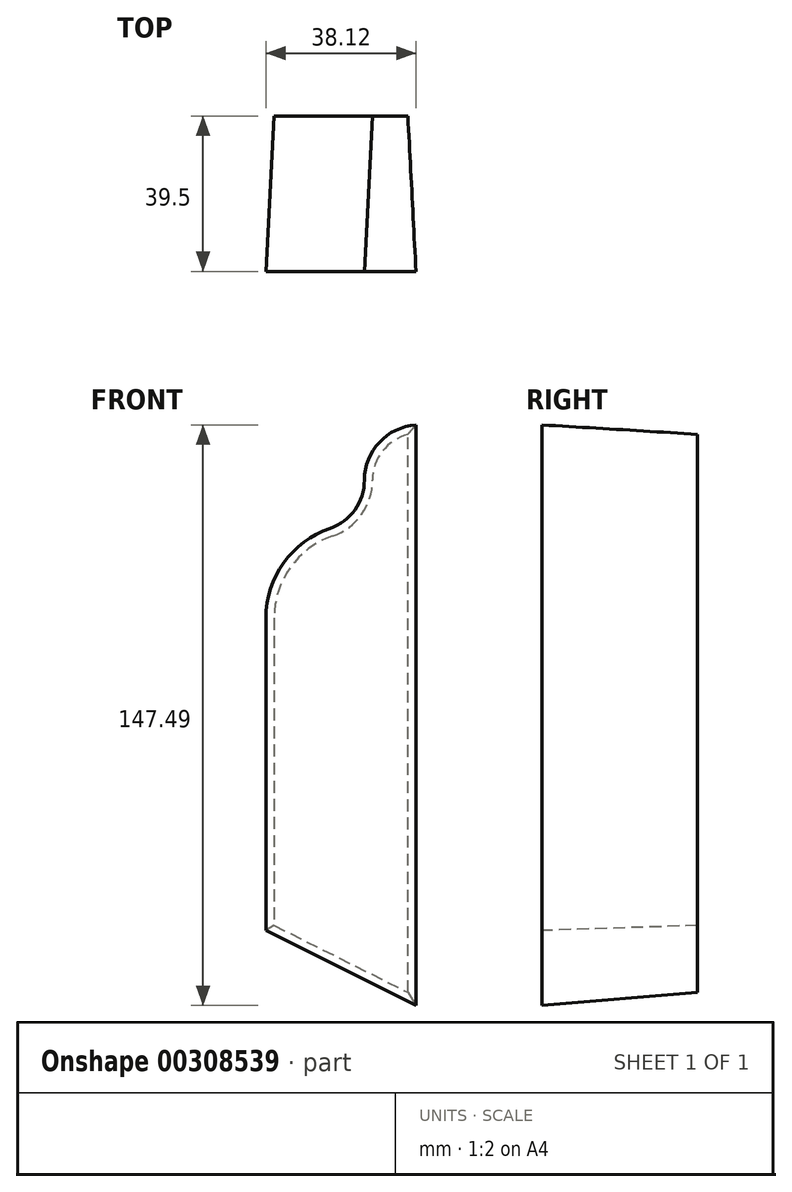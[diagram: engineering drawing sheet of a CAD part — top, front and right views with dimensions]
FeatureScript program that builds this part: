
annotation { "Feature Type Name" : "Feature", "Feature Type Description" : "" }
export const myFeature = defineFeature(function(context is Context, id is Id, definition is map)
    precondition{}
    {
        {
            var Q0;
            Q0=qCreatedBy(makeId("Front.planeOp"),FACE);
            var sketch = newSketch(context, id + "F0", { "sketchPlane" : qUnion([Q0])});
            skLineSegment(sketch, "E0", {"start": v(0, -48.23) * mm, "end": v(0, 136.3) * mm, "construction": true});
            skLineSegment(sketch, "E1", {"start": v(40, 0) * mm, "end": v(40, 80) * mm});
            skArc(sketch, "E2", {"start": v(40, 80) * mm, "mid": v(35.34, 94.53) * mm, "end": v(23.1, 103.65) * mm});
            skArc(sketch, "E3", {"start": v(23.1, 103.65) * mm, "mid": v(17.24, 108.03) * mm, "end": v(15, 115) * mm});
            skArc(sketch, "E4", {"start": v(15, 115) * mm, "mid": v(10.6, 125.6) * mm, "end": v(0, 130) * mm});
            skLineSegment(sketch, "E5", {"start": v(0, -20) * mm, "end": v(40, 0) * mm});
            skLineSegment(sketch, "E6", {"start": v(0, 130) * mm, "end": v(0, -20) * mm});
            skArc(sketch, "E7.MirrorCS", {"start": v(-23.1, 103.65) * mm, "mid": v(-17.24, 108.03) * mm, "end": v(-15, 115) * mm});
            skArc(sketch, "E8.MirrorCS", {"start": v(-40, 80) * mm, "mid": v(-35.34, 94.53) * mm, "end": v(-23.1, 103.65) * mm});
            skLineSegment(sketch, "E9.MirrorCS", {"start": v(-40, 0) * mm, "end": v(-40, 80) * mm});
            skLineSegment(sketch, "E10.MirrorCS", {"start": v(0, -20) * mm, "end": v(-40, 0) * mm});
            skArc(sketch, "E11.MirrorCS", {"start": v(-15, 115) * mm, "mid": v(-10.6, 125.6) * mm, "end": v(0, 130) * mm});
            skSolve(sketch);
        }
        {
            var Q0;
            Q0=makeQuery(id+"F0.imprint","IMPRINT",FACE,{"disambiguationData":[TD([[makeQuery(id+"F0.imprint","IMPRINT",EDGE,{"derivedFrom":sQuery(id+"F0.wireOp",EDGE,"E6")}),-1.0]])]});
            extrude(context, id + "F1", {"entities" : qUnion([Q0]), "oppositeDirection" : true, "depth" : 57.5 * mm, "hasDraft" : true, "draftAngle" : 3 * degree, "draftPullDirection" : true, "hasSecondDirection" : true, "secondDirectionOppositeDirection" : true, "secondDirectionDepth" : 18 * mm, "hasSecondDirectionDraft" : true, "secondDirectionDraftAngle" : 10 * degree, "secondDirectionDraftPullDirection" : true});
        }
    });
